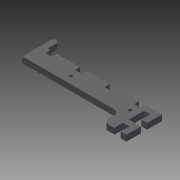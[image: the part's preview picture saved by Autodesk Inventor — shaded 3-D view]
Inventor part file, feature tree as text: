
AUTODESK INVENTOR PART (.ipt)
format: ipt  version: 2013 (Build 170138000, 138)  size: 121,856 bytes
history: native  units: mm
features: extrude x1, sketch x1
ambient origin geometry x8: Origin, YZ Plane, XZ Plane, XY Plane, X Axis, Y Axis, Z Axis, Center Point
bodies: Solid1 (feature_tree)
feature tree (2):
  extrude  "Extrusion1"  [1 undecoded]
  sketch  "Sketch1"  dims[d0=6.0mm d1=0.0mm]
note: 1 required parameter value undecoded (feature->parameter linkage not recoverable at this tier; creation-order binding heuristic only, values carry confidence <= 0.55)
